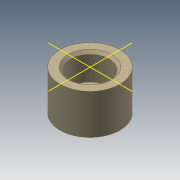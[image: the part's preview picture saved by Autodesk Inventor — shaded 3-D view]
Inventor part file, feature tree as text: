
AUTODESK INVENTOR PART (.ipt)
format: ipt  version: 2020.3 (Build 243373000, 373)  size: 109,568 bytes
history: native  units: in
note: dims shown in document units (in); Inventor stores cm internally (conversion verified against a paired STEP export)
features: sketch x3, extrude x1, hole x1, chamfer x1
ambient origin geometry x8: Origin, YZ Plane, XZ Plane, XY Plane, X Axis, Y Axis, Z Axis, Center Point
bodies: Solid1 (feature_tree)
feature tree (6):
  extrude  "Extrusion1"  Depth=0.75in TaperAngle=0.0deg
  sketch  "Sketch2"  dims[d3=0.25in d4=0.75in d5=0.72in d6=0.5in d7=90.0deg d8=1.0in d9=0.8108in d10=0.05in d11=0.125in d12=45.0deg]
  hole  "Hole1"  [1 undecoded]
  chamfer  "Chamfer1"  [1 undecoded]
  sketch  "Sketch1"  dims[d0=1.125in d1=0.75in d2=0.0in]
  sketch  "Sketch3"
note: 2 required parameter values undecoded (feature->parameter linkage not recoverable at this tier; creation-order binding heuristic only, values carry confidence <= 0.55)
